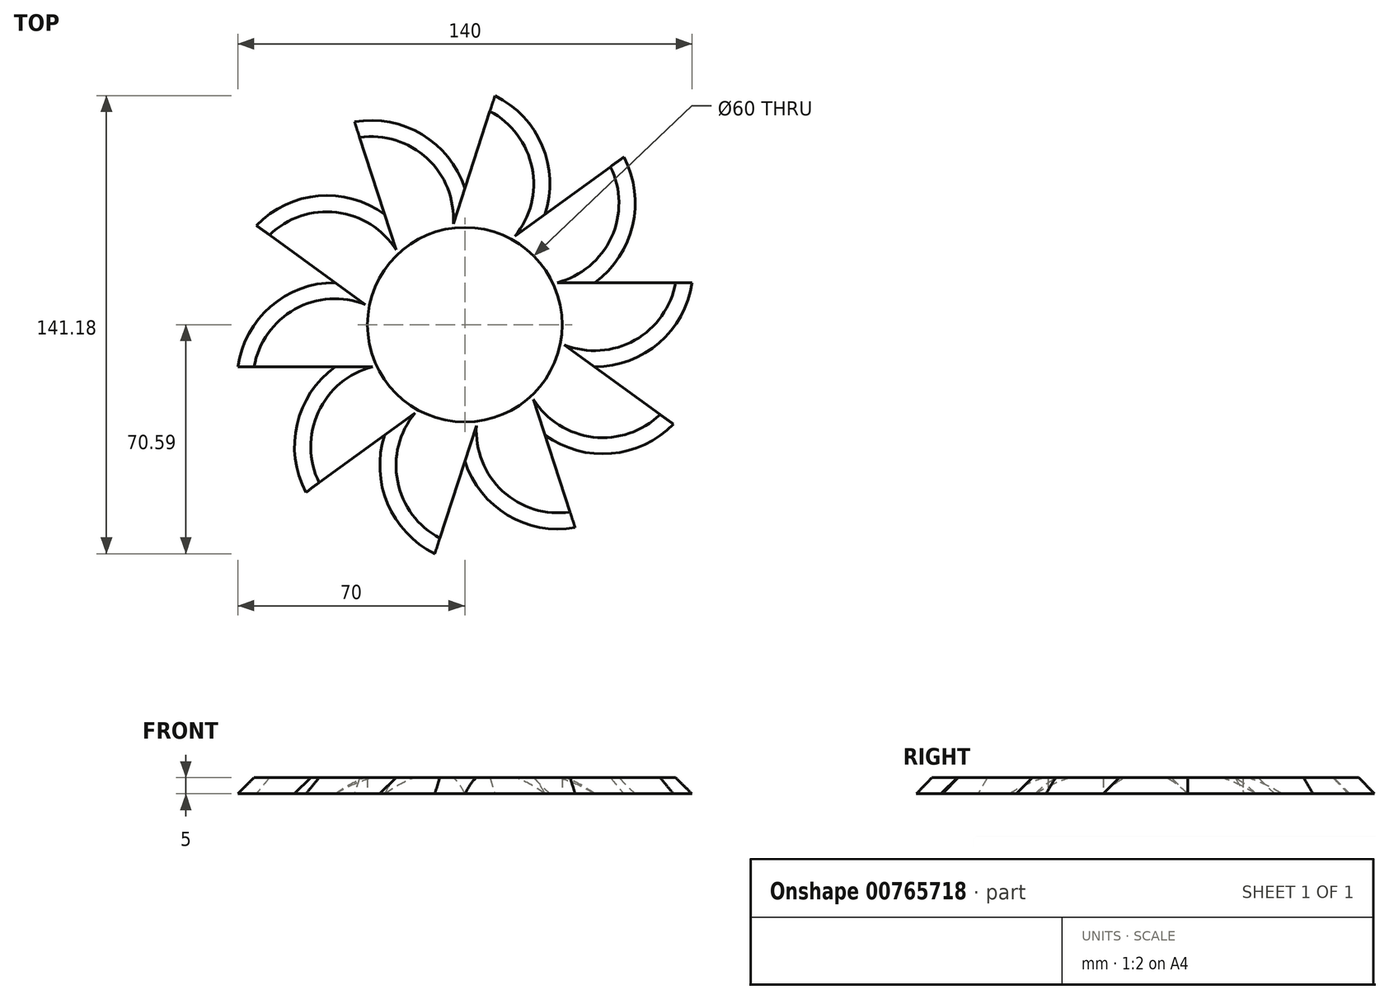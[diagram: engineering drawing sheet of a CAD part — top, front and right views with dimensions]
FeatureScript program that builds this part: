
annotation { "Feature Type Name" : "Feature", "Feature Type Description" : "" }
export const myFeature = defineFeature(function(context is Context, id is Id, definition is map)
    precondition{}
    {
        {
            var Q0;
            Q0=qCreatedBy(makeId("Top.planeOp"),FACE);
            var sketch = newSketch(context, id + "F0", { "sketchPlane" : qUnion([Q0])});
            skCircle(sketch, "E0.cCircle", {"center": v(0, 0) * mm, "radius": 40 * mm, "construction": true});
            skLineSegment(sketch, "E0.0", {"start": v(40, 13) * mm, "end": v(40, -13) * mm});
            skLineSegment(sketch, "E0.1", {"start": v(40, -13) * mm, "end": v(24.72, -34.03) * mm});
            skLineSegment(sketch, "E0.2", {"start": v(24.72, -34.03) * mm, "end": v(0, -42.06) * mm});
            skLineSegment(sketch, "E0.3", {"start": v(0, -42.06) * mm, "end": v(-24.72, -34.03) * mm});
            skLineSegment(sketch, "E0.4", {"start": v(-24.72, -34.03) * mm, "end": v(-40, -13) * mm});
            skLineSegment(sketch, "E0.5", {"start": v(-40, -13) * mm, "end": v(-40, 13) * mm});
            skLineSegment(sketch, "E0.6", {"start": v(-40, 13) * mm, "end": v(-24.72, 34.03) * mm});
            skLineSegment(sketch, "E0.7", {"start": v(-24.72, 34.03) * mm, "end": v(0, 42.06) * mm});
            skLineSegment(sketch, "E0.8", {"start": v(0, 42.06) * mm, "end": v(24.72, 34.03) * mm});
            skLineSegment(sketch, "E0.9", {"start": v(24.72, 34.03) * mm, "end": v(40, 13) * mm});
            skPoint(sketch, "E0.0.midPoint", {"position": v(40, 0) * mm});
            skLineSegment(sketch, "E1", {"start": v(0, 42.06) * mm, "end": v(9.27, 70.6) * mm, "construction": true});
            skLineSegment(sketch, "E2", {"start": v(9.27, 70.6) * mm, "end": v(34, 62.56) * mm, "construction": true});
            skLineSegment(sketch, "E3", {"start": v(34, 62.56) * mm, "end": v(24.72, 34.03) * mm, "construction": true});
            skLineSegment(sketch, "E4", {"start": v(9.27, 70.6) * mm, "end": v(0, 42.06) * mm});
            skArc(sketch, "E5", {"start": v(24.72, 34.03) * mm, "mid": v(23.81, 55.19) * mm, "end": v(9.27, 70.6) * mm});
            skArc(sketch, "E6.1.0", {"start": v(0, 42.06) * mm, "mid": v(-13.17, 58.65) * mm, "end": v(-34, 62.56) * mm});
            skLineSegment(sketch, "E6.1.1", {"start": v(-34, 62.56) * mm, "end": v(-24.72, 34.03) * mm});
            skArc(sketch, "E6.2.0", {"start": v(-24.72, 34.03) * mm, "mid": v(-45.13, 39.7) * mm, "end": v(-64.27, 30.63) * mm});
            skLineSegment(sketch, "E6.2.1", {"start": v(-64.27, 30.63) * mm, "end": v(-40, 13) * mm});
            skArc(sketch, "E6.3.0", {"start": v(-40, 13) * mm, "mid": v(-59.85, 5.6) * mm, "end": v(-70, -13) * mm});
            skLineSegment(sketch, "E6.3.1", {"start": v(-70, -13) * mm, "end": v(-40, -13) * mm});
            skArc(sketch, "E6.4.0", {"start": v(-40, -13) * mm, "mid": v(-51.7, -30.65) * mm, "end": v(-49, -51.66) * mm});
            skLineSegment(sketch, "E6.4.1", {"start": v(-49, -51.66) * mm, "end": v(-24.72, -34.03) * mm});
            skArc(sketch, "E6.5.0", {"start": v(-24.72, -34.03) * mm, "mid": v(-23.81, -55.19) * mm, "end": v(-9.27, -70.6) * mm});
            skLineSegment(sketch, "E6.5.1", {"start": v(-9.27, -70.6) * mm, "end": v(0, -42.06) * mm});
            skArc(sketch, "E6.6.0", {"start": v(0, -42.06) * mm, "mid": v(13.17, -58.65) * mm, "end": v(34, -62.56) * mm});
            skLineSegment(sketch, "E6.6.1", {"start": v(34, -62.56) * mm, "end": v(24.72, -34.03) * mm});
            skArc(sketch, "E6.7.0", {"start": v(24.72, -34.03) * mm, "mid": v(45.13, -39.7) * mm, "end": v(64.27, -30.63) * mm});
            skLineSegment(sketch, "E6.7.1", {"start": v(64.27, -30.63) * mm, "end": v(40, -13) * mm});
            skArc(sketch, "E6.8.0", {"start": v(40, -13) * mm, "mid": v(59.85, -5.6) * mm, "end": v(70, 13) * mm});
            skLineSegment(sketch, "E6.8.1", {"start": v(70, 13) * mm, "end": v(40, 13) * mm});
            skArc(sketch, "E6.9.0", {"start": v(40, 13) * mm, "mid": v(51.7, 30.65) * mm, "end": v(49, 51.66) * mm});
            skLineSegment(sketch, "E6.9.1", {"start": v(49, 51.66) * mm, "end": v(24.72, 34.03) * mm});
            skCircle(sketch, "E7", {"center": v(0, 0) * mm, "radius": 30 * mm});
            skSolve(sketch);
        }
        {
            var Q0;
            Q0=makeQuery(id+"F0.imprint","IMPRINT",FACE,{"disambiguationData":[TD([[makeQuery(id+"F0.imprint","IMPRINT",EDGE,{"derivedFrom":sQuery(id+"F0.wireOp",EDGE,"E6.2.0")}),1.0]])]});
            var Q1;
            Q1=makeQuery(id+"F0.imprint","IMPRINT",FACE,{"disambiguationData":[TD([[makeQuery(id+"F0.imprint","IMPRINT",EDGE,{"derivedFrom":sQuery(id+"F0.wireOp",EDGE,"E0.8")}),-1.0]])]});
            var Q2;
            Q2=makeQuery(id+"F0.imprint","IMPRINT",FACE,{"disambiguationData":[TD([[makeQuery(id+"F0.imprint","IMPRINT",EDGE,{"derivedFrom":sQuery(id+"F0.wireOp",EDGE,"E6.1.0")}),1.0]])]});
            var Q3;
            Q3=makeQuery(id+"F0.imprint","IMPRINT",FACE,{"disambiguationData":[TD([[makeQuery(id+"F0.imprint","IMPRINT",EDGE,{"derivedFrom":sQuery(id+"F0.wireOp",EDGE,"E0.8")}),1.0]])]});
            var Q4;
            Q4=makeQuery(id+"F0.imprint","IMPRINT",FACE,{"disambiguationData":[TD([[makeQuery(id+"F0.imprint","IMPRINT",EDGE,{"derivedFrom":sQuery(id+"F0.wireOp",EDGE,"E6.9.0")}),1.0]])]});
            var Q5;
            Q5=makeQuery(id+"F0.imprint","IMPRINT",FACE,{"disambiguationData":[TD([[makeQuery(id+"F0.imprint","IMPRINT",EDGE,{"derivedFrom":sQuery(id+"F0.wireOp",EDGE,"E6.8.0")}),1.0]])]});
            var Q6;
            Q6=makeQuery(id+"F0.imprint","IMPRINT",FACE,{"disambiguationData":[TD([[makeQuery(id+"F0.imprint","IMPRINT",EDGE,{"derivedFrom":sQuery(id+"F0.wireOp",EDGE,"E6.7.0")}),1.0]])]});
            var Q7;
            Q7=makeQuery(id+"F0.imprint","IMPRINT",FACE,{"disambiguationData":[TD([[makeQuery(id+"F0.imprint","IMPRINT",EDGE,{"derivedFrom":sQuery(id+"F0.wireOp",EDGE,"E6.6.0")}),1.0]])]});
            var Q8;
            Q8=makeQuery(id+"F0.imprint","IMPRINT",FACE,{"disambiguationData":[TD([[makeQuery(id+"F0.imprint","IMPRINT",EDGE,{"derivedFrom":sQuery(id+"F0.wireOp",EDGE,"E6.5.0")}),1.0]])]});
            var Q9;
            Q9=makeQuery(id+"F0.imprint","IMPRINT",FACE,{"disambiguationData":[TD([[makeQuery(id+"F0.imprint","IMPRINT",EDGE,{"derivedFrom":sQuery(id+"F0.wireOp",EDGE,"E6.4.0")}),1.0]])]});
            var Q10;
            Q10=makeQuery(id+"F0.imprint","IMPRINT",FACE,{"disambiguationData":[TD([[makeQuery(id+"F0.imprint","IMPRINT",EDGE,{"derivedFrom":sQuery(id+"F0.wireOp",EDGE,"E6.3.0")}),1.0]])]});
            extrude(context, id + "F1", {"entities" : qUnion([Q0, Q1, Q2, Q3, Q4, Q5, Q6, Q7, Q8, Q9, Q10]), "depth" : 5 * mm, "offsetDistance" : 25 * mm});
        }
        {
            var Q0;
            Q0=makeQuery(id+"F1.opExtrude","CAP_EDGE",EDGE,{"disambiguationData":[OSD([sQuery(id+"F0.wireOp",EDGE,"E6.5.0")])],"isStart":false});
            var Q1;
            Q1=makeQuery(id+"F1.opExtrude","CAP_EDGE",EDGE,{"disambiguationData":[OSD([sQuery(id+"F0.wireOp",EDGE,"E6.4.0")])],"isStart":false});
            var Q2;
            Q2=makeQuery(id+"F1.opExtrude","CAP_EDGE",EDGE,{"disambiguationData":[OSD([sQuery(id+"F0.wireOp",EDGE,"E6.3.0")])],"isStart":false});
            var Q3;
            Q3=makeQuery(id+"F1.opExtrude","CAP_EDGE",EDGE,{"disambiguationData":[OSD([sQuery(id+"F0.wireOp",EDGE,"E6.2.0")])],"isStart":false});
            var Q4;
            Q4=makeQuery(id+"F1.opExtrude","CAP_EDGE",EDGE,{"disambiguationData":[OSD([sQuery(id+"F0.wireOp",EDGE,"E6.1.0")])],"isStart":false});
            var Q5;
            Q5=makeQuery(id+"F1.opExtrude","CAP_EDGE",EDGE,{"disambiguationData":[OSD([sQuery(id+"F0.wireOp",EDGE,"E5")])],"isStart":false});
            var Q6;
            Q6=makeQuery(id+"F1.opExtrude","CAP_EDGE",EDGE,{"disambiguationData":[OSD([sQuery(id+"F0.wireOp",EDGE,"E6.9.0")])],"isStart":false});
            var Q7;
            Q7=makeQuery(id+"F1.opExtrude","CAP_EDGE",EDGE,{"disambiguationData":[OSD([sQuery(id+"F0.wireOp",EDGE,"E6.8.0")])],"isStart":false});
            var Q8;
            Q8=makeQuery(id+"F1.opExtrude","CAP_EDGE",EDGE,{"disambiguationData":[OSD([sQuery(id+"F0.wireOp",EDGE,"E6.7.0")])],"isStart":false});
            var Q9;
            Q9=makeQuery(id+"F1.opExtrude","CAP_EDGE",EDGE,{"disambiguationData":[OSD([sQuery(id+"F0.wireOp",EDGE,"E6.6.0")])],"isStart":false});
            chamfer(context, id + "F2", {"entities" : qUnion([Q0, Q1, Q2, Q3, Q4, Q5, Q6, Q7, Q8, Q9]), "width" : 5 * mm, "tangentPropagation" : true});
        }
    });
